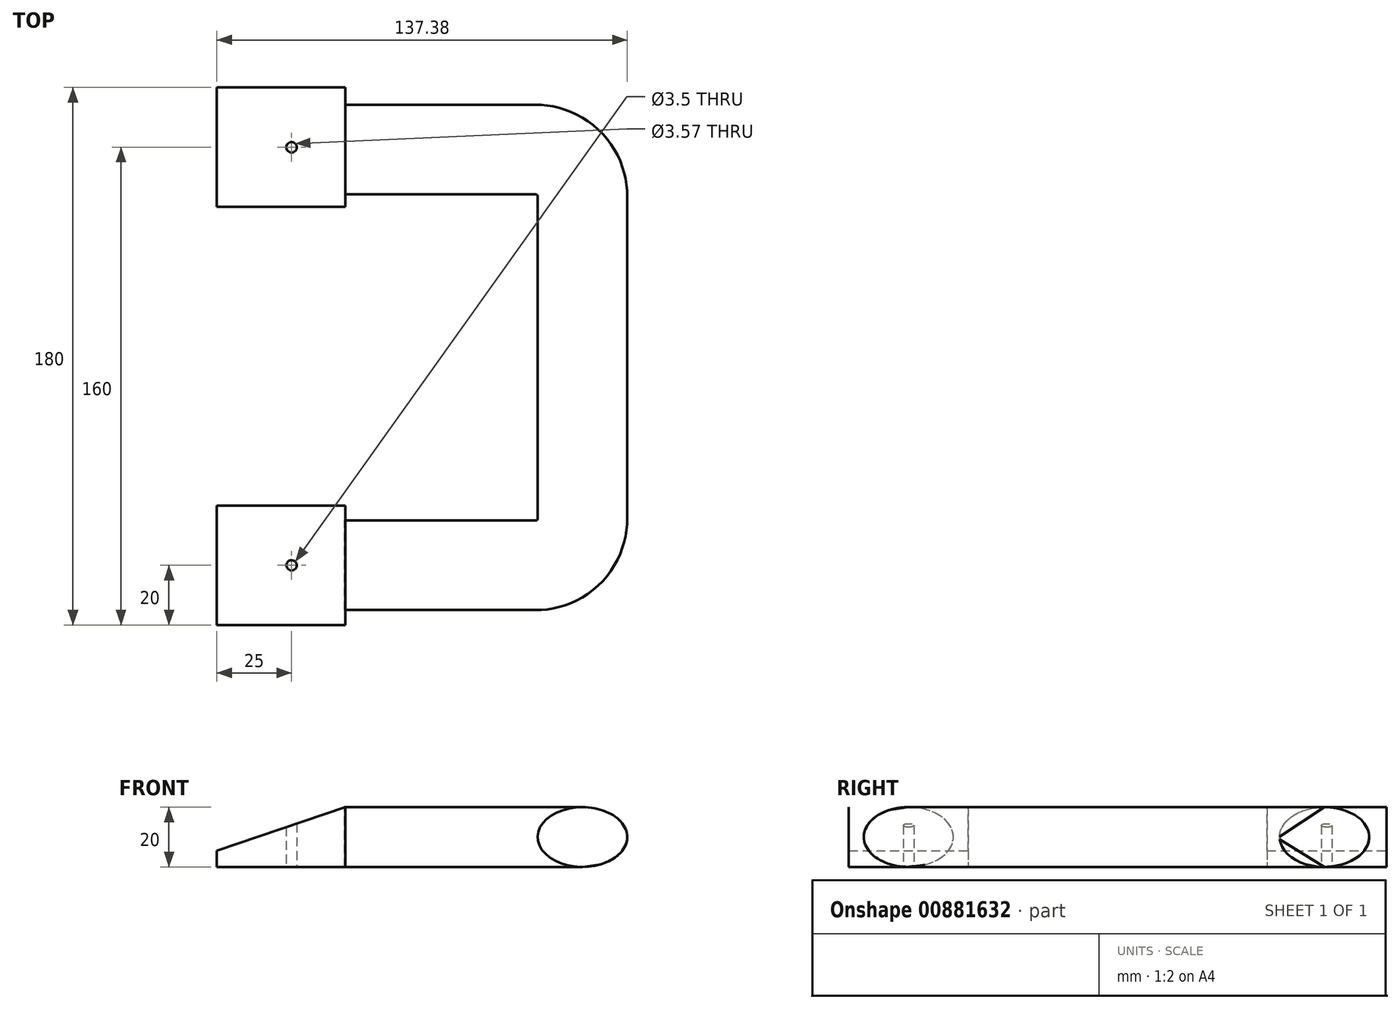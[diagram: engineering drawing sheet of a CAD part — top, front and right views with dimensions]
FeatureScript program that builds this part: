
annotation { "Feature Type Name" : "Feature", "Feature Type Description" : "" }
export const myFeature = defineFeature(function(context is Context, id is Id, definition is map)
    precondition{}
    {
        {
            var Q0;
            Q0=qCreatedBy(makeId("Front.planeOp"),FACE);
            var sketch = newSketch(context, id + "F0", { "sketchPlane" : qUnion([Q0])});
            skLineSegment(sketch, "E0.left", {"start": v(-28, 61.6) * mm, "end": v(-28, 47) * mm});
            skPoint(sketch, "E0.middle", {"position": v(-49.5, 54.3) * mm});
            skLineSegment(sketch, "E1", {"start": v(-71, 47) * mm, "end": v(-28, 61.6) * mm});
            skLineSegment(sketch, "E2.top", {"start": v(-71, 41.6) * mm, "end": v(-28, 41.6) * mm});
            skLineSegment(sketch, "E2.left", {"start": v(-71, 47) * mm, "end": v(-71, 41.6) * mm});
            skLineSegment(sketch, "E2.right", {"start": v(-28, 47) * mm, "end": v(-28, 41.6) * mm});
            skSolve(sketch);
        }
        {
            var Q0;
            Q0=makeQuery(id+"F0.imprint","IMPRINT",FACE,{"disambiguationData":[TD([[makeQuery(id+"F0.imprint","IMPRINT",EDGE,{"derivedFrom":sQuery(id+"F0.wireOp",EDGE,"E0.left")}),-1.0]])]});
            extrude(context, id + "F1", {"entities" : qUnion([Q0]), "depth" : 40 * mm, "offsetDistance" : 25 * mm});
        }
        {
            var Q0;
            Q0=qCreatedBy(makeId("Front.planeOp"),FACE);
            cPlane(context, id + "F2", {"entities" : qUnion([Q0]), "cplaneType" : CPlaneType.OFFSET, "offset" : 140 * mm, "width" : 150 * mm, "height" : 150 * mm});
        }
        {
            var Q0;
            Q0=qCreatedBy(id+"F2.planeOp",FACE);
            var sketch = newSketch(context, id + "F3", { "sketchPlane" : qUnion([Q0])});
            skLineSegment(sketch, "E3.left", {"start": v(-28, 61.6) * mm, "end": v(-28, 47) * mm});
            skPoint(sketch, "E3.middle", {"position": v(-49.5, 54.3) * mm});
            skLineSegment(sketch, "E4", {"start": v(-71, 47) * mm, "end": v(-28, 61.6) * mm});
            skLineSegment(sketch, "E5.top", {"start": v(-71, 41.6) * mm, "end": v(-28, 41.6) * mm});
            skLineSegment(sketch, "E5.left", {"start": v(-71, 47) * mm, "end": v(-71, 41.6) * mm});
            skLineSegment(sketch, "E5.right", {"start": v(-28, 47) * mm, "end": v(-28, 41.6) * mm});
            skSolve(sketch);
        }
        {
            var Q0;
            Q0=makeQuery(id+"F3.imprint","IMPRINT",FACE,{"disambiguationData":[TD([[makeQuery(id+"F3.imprint","IMPRINT",EDGE,{"derivedFrom":sQuery(id+"F3.wireOp",EDGE,"E3.left")}),-1.0]])]});
            extrude(context, id + "F4", {"entities" : qUnion([Q0]), "depth" : 40 * mm, "offsetDistance" : 25 * mm});
        }
        {
            var Q0;
            Q0=makeQuery(id+"F4.opExtrude","SWEPT_FACE",FACE,{"disambiguationData":[OSD([sQuery(id+"F3.wireOp",EDGE,"E3.left")])]});
            var sketch = newSketch(context, id + "F5", { "sketchPlane" : qUnion([Q0])});
            skEllipse(sketch, "E6", {"center": v(-160, 51.6) * mm, "majorRadius": 15 * mm, "minorRadius": 10 * mm, "majorAxis": v(-1, 0)});
            skSolve(sketch);
        }
        {
            var Q0;
            Q0=makeQuery(id+"F4.opExtrude","SWEPT_FACE",FACE,{"disambiguationData":[OSD([sQuery(id+"F3.wireOp",EDGE,"E5.top")])]});
            cPlane(context, id + "F6", {"entities" : qUnion([Q0]), "cplaneType" : CPlaneType.OFFSET, "offset" : 10 * mm, "oppositeDirection" : true, "width" : 150 * mm, "height" : 150 * mm});
        }
        {
            var Q0;
            Q0=qCreatedBy(id+"F6.planeOp",FACE);
            var sketch = newSketch(context, id + "F7", { "sketchPlane" : qUnion([Q0])});
            skLineSegment(sketch, "E7", {"start": v(-28.23, 160.4) * mm, "end": v(35.77, 160.4) * mm});
            skLineSegment(sketch, "E8", {"start": v(51.77, 144.4) * mm, "end": v(51.77, 36.4) * mm});
            skLineSegment(sketch, "E9", {"start": v(35.77, 20.4) * mm, "end": v(-28.23, 20.4) * mm});
            skPoint(sketch, "E10.visualSharp", {"position": v(51.77, 160.4) * mm});
            skArc(sketch, "E10.filletArc", {"start": v(51.77, 144.4) * mm, "mid": v(47.09, 155.7) * mm, "end": v(35.77, 160.4) * mm});
            skPoint(sketch, "E11.visualSharp", {"position": v(51.77, 20.4) * mm});
            skArc(sketch, "E11.filletArc", {"start": v(35.77, 20.4) * mm, "mid": v(47.09, 25.08) * mm, "end": v(51.77, 36.4) * mm});
            skSolve(sketch);
        }
        {
            var Q0;
            {var subQ0=sQuery(id+"F5.wireOp",EDGE,"E6");var subQ1=makeQuery(id+"F5.imprint","INTERSECT",VERTEX,{"derivedFrom":[makeQuery(id+"F4.opExtrude","SWEPT_EDGE",EDGE,{"disambiguationData":[OSD([sQuery(id+"F3.wireOp",EDGE,"E3.left"),sQuery(id+"F3.wireOp",EDGE,"E4")])]}),subQ0]});Q0=makeQuery(id+"F5.imprint","IMPRINT",FACE,{"disambiguationData":[TD([[makeQuery(id+"F5.imprint","IMPRINT",EDGE,{"disambiguationData":[TD([[subQ1,1.0]])],"derivedFrom":subQ0}),1.0]])]});}
            var Q1;
            Q1=sQuery(id+"F7.wireOp",EDGE,"E7");
            var Q2;
            Q2=sQuery(id+"F7.wireOp",EDGE,"E10.filletArc");
            var Q3;
            Q3=sQuery(id+"F7.wireOp",EDGE,"E8");
            var Q4;
            Q4=sQuery(id+"F7.wireOp",EDGE,"E11.filletArc");
            var Q5;
            Q5=sQuery(id+"F7.wireOp",EDGE,"E9");
            sweep(context, id + "F8", {"profiles" : qUnion([Q0]), "path" : qUnion([Q1, Q2, Q3, Q4, Q5])});
        }
        {
            var Q0;
            Q0=makeQuery(id+"F4.opExtrude","SWEPT_FACE",FACE,{"disambiguationData":[OSD([sQuery(id+"F3.wireOp",EDGE,"E5.top")])]});
            cPlane(context, id + "F9", {"entities" : qUnion([Q0]), "cplaneType" : CPlaneType.OFFSET, "offset" : 0 * mm, "width" : 150 * mm, "height" : 150 * mm});
        }
        {
            var Q0;
            Q0=qCreatedBy(id+"F9.planeOp",FACE);
            var sketch = newSketch(context, id + "F10", { "sketchPlane" : qUnion([Q0])});
            skCircle(sketch, "E12", {"center": v(-46, 160) * mm, "radius": 1.75 * mm});
            skCircle(sketch, "E13", {"center": v(-46, 20) * mm, "radius": 1.78 * mm});
            skSolve(sketch);
        }
        {
            var Q0;
            Q0 = qSketchRegion(id + "F10", true);
            extrude(context, id + "F11", {"entities" : qUnion([Q0]), "operationType" : NewBodyOperationType.REMOVE, "oppositeDirection" : true, "depth" : 25 * mm, "offsetDistance" : 25 * mm});
        }
    });
